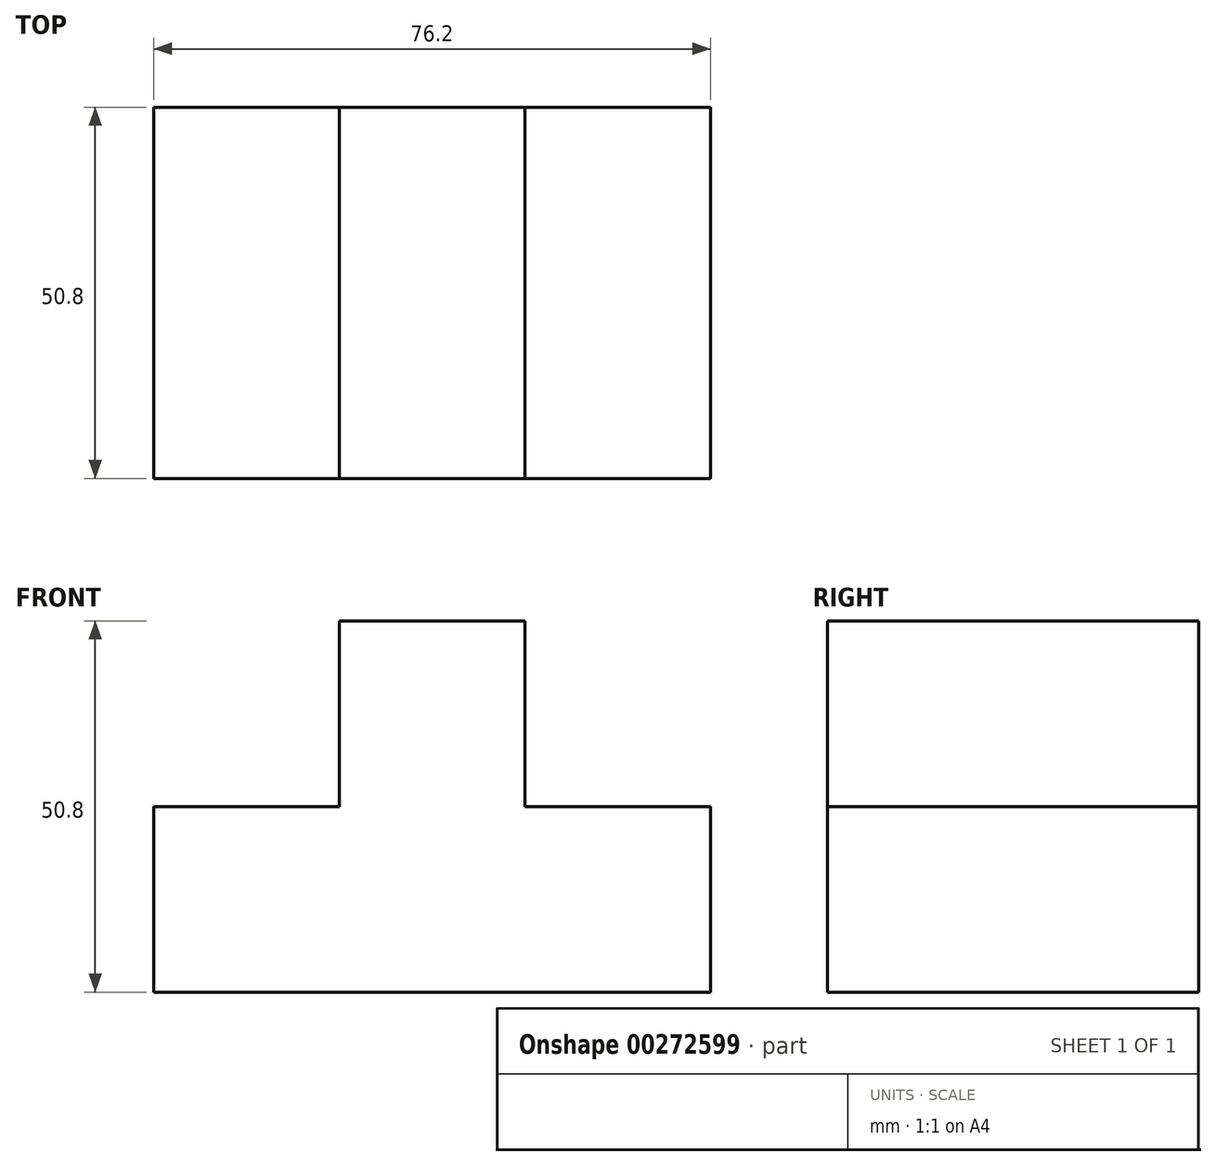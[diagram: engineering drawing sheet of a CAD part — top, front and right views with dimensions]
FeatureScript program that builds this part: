
annotation { "Feature Type Name" : "Feature", "Feature Type Description" : "" }
export const myFeature = defineFeature(function(context is Context, id is Id, definition is map)
    precondition{}
    {
        {
            var Q0;
            Q0=qCreatedBy(makeId("Front.planeOp"),FACE);
            var sketch = newSketch(context, id + "F0", { "sketchPlane" : qUnion([Q0])});
            skLineSegment(sketch, "E0", {"start": v(0, 0) * mm, "end": v(0, 25.4) * mm});
            skLineSegment(sketch, "E1", {"start": v(0, 25.4) * mm, "end": v(25.4, 25.4) * mm});
            skLineSegment(sketch, "E2", {"start": v(25.4, 25.4) * mm, "end": v(25.4, 50.8) * mm});
            skLineSegment(sketch, "E3", {"start": v(25.4, 50.8) * mm, "end": v(50.8, 50.8) * mm});
            skLineSegment(sketch, "E4", {"start": v(50.8, 50.8) * mm, "end": v(50.8, 25.4) * mm});
            skLineSegment(sketch, "E5", {"start": v(50.8, 25.4) * mm, "end": v(76.2, 25.4) * mm});
            skLineSegment(sketch, "E6", {"start": v(76.2, 25.4) * mm, "end": v(76.2, 0) * mm});
            skLineSegment(sketch, "E7", {"start": v(76.2, 0) * mm, "end": v(0, 0) * mm});
            skSolve(sketch);
        }
        {
            var Q0;
            Q0=makeQuery(id+"F0.imprint","IMPRINT",FACE,{"disambiguationData":[TD([[makeQuery(id+"F0.imprint","IMPRINT",EDGE,{"derivedFrom":sQuery(id+"F0.wireOp",EDGE,"E0")}),-1.0]])]});
            extrude(context, id + "F1", {"entities" : qUnion([Q0]), "depth" : 50.8 * mm});
        }
    });
